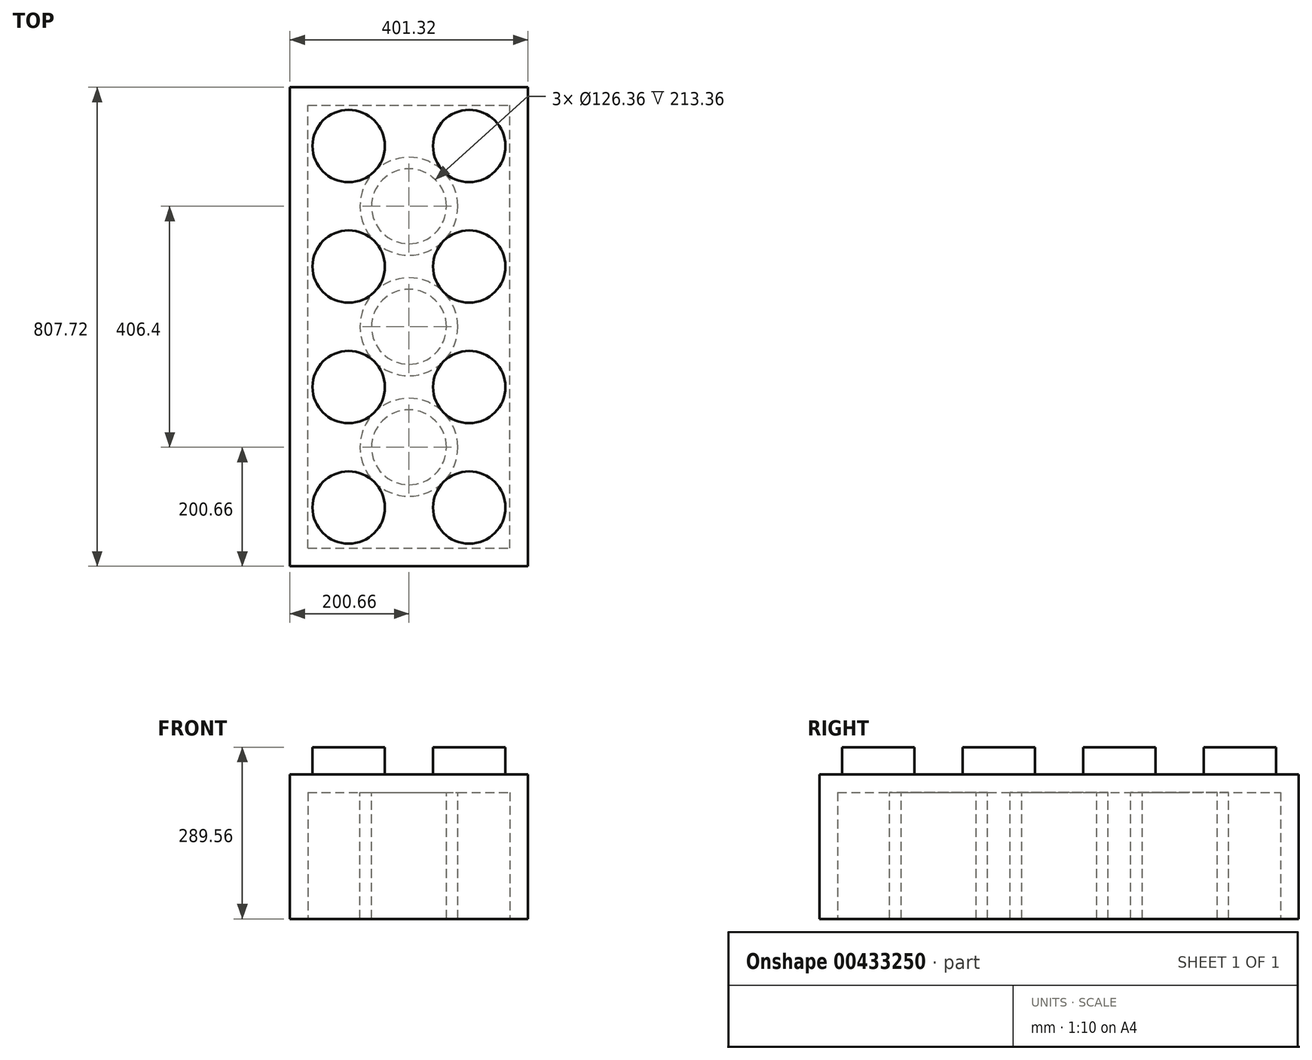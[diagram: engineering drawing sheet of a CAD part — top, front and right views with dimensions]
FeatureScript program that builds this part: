
annotation { "Feature Type Name" : "Feature", "Feature Type Description" : "" }
export const myFeature = defineFeature(function(context is Context, id is Id, definition is map)
    precondition{}
    {
        {
            var Q0;
            Q0=qCreatedBy(makeId("Top.planeOp"),FACE);
            var sketch = newSketch(context, id + "F0", { "sketchPlane" : qUnion([Q0])});
            skLineSegment(sketch, "E0.bottom", {"start": v(-200.66, -403.86) * mm, "end": v(200.66, -403.86) * mm});
            skLineSegment(sketch, "E0.top", {"start": v(-200.66, 403.86) * mm, "end": v(200.66, 403.86) * mm});
            skLineSegment(sketch, "E0.left", {"start": v(-200.66, -403.86) * mm, "end": v(-200.66, 403.86) * mm});
            skLineSegment(sketch, "E0.right", {"start": v(200.66, -403.86) * mm, "end": v(200.66, 403.86) * mm});
            skPoint(sketch, "E0.middle", {"position": v(0, 0) * mm});
            skSolve(sketch);
        }
        {
            var Q0;
            Q0 = qSketchRegion(id + "F0", true);
            extrude(context, id + "F1", {"entities" : qUnion([Q0]), "depth" : 243.84 * mm});
        }
        {
            var Q0;
            Q0=makeQuery(id+"F1.opExtrude","CAP_FACE",FACE,{"disambiguationData":[OSD([sQuery(id+"F0.wireOp",EDGE,"E0.bottom"),sQuery(id+"F0.wireOp",EDGE,"E0.top"),sQuery(id+"F0.wireOp",EDGE,"E0.left"),sQuery(id+"F0.wireOp",EDGE,"E0.right")])],"isStart":false});
            var sketch = newSketch(context, id + "F2", { "sketchPlane" : qUnion([Q0])});
            skCircle(sketch, "E1", {"center": v(101.6, 304.8) * mm, "radius": 60.96 * mm});
            skCircle(sketch, "E2.0.1.0", {"center": v(101.6, 101.6) * mm, "radius": 60.96 * mm});
            skCircle(sketch, "E2.0.2.0", {"center": v(101.6, -101.6) * mm, "radius": 60.96 * mm});
            skCircle(sketch, "E2.0.3.0", {"center": v(101.6, -304.8) * mm, "radius": 60.96 * mm});
            skCircle(sketch, "E2.1.0.0", {"center": v(-101.6, 304.8) * mm, "radius": 60.96 * mm});
            skCircle(sketch, "E2.1.1.0", {"center": v(-101.6, 101.6) * mm, "radius": 60.96 * mm});
            skCircle(sketch, "E2.1.2.0", {"center": v(-101.6, -101.6) * mm, "radius": 60.96 * mm});
            skCircle(sketch, "E2.1.3.0", {"center": v(-101.6, -304.8) * mm, "radius": 60.96 * mm});
            skLineSegment(sketch, "E2.direction1", {"start": v(101.6, 304.8) * mm, "end": v(-101.6, 304.8) * mm, "construction": true});
            skLineSegment(sketch, "E2.direction2", {"start": v(101.6, 304.8) * mm, "end": v(101.6, 101.6) * mm, "construction": true});
            skSolve(sketch);
        }
        {
            var Q0;
            Q0 = qSketchRegion(id + "F2", true);
            extrude(context, id + "F3", {"entities" : qUnion([Q0]), "operationType" : NewBodyOperationType.ADD, "depth" : 45.72 * mm});
        }
        {
            var Q0;
            Q0=makeQuery(id+"F1.opExtrude","CAP_FACE",FACE,{"disambiguationData":[OSD([sQuery(id+"F0.wireOp",EDGE,"E0.bottom"),sQuery(id+"F0.wireOp",EDGE,"E0.top"),sQuery(id+"F0.wireOp",EDGE,"E0.left"),sQuery(id+"F0.wireOp",EDGE,"E0.right")])],"isStart":true});
            var sketch = newSketch(context, id + "F4", { "sketchPlane" : qUnion([Q0])});
            skLineSegment(sketch, "E3.bottom", {"start": v(-170.18, 373.38) * mm, "end": v(170.18, 373.38) * mm});
            skLineSegment(sketch, "E3.top", {"start": v(-170.18, -373.38) * mm, "end": v(170.18, -373.38) * mm});
            skLineSegment(sketch, "E3.left", {"start": v(-170.18, 373.38) * mm, "end": v(-170.18, -373.38) * mm});
            skLineSegment(sketch, "E3.right", {"start": v(170.18, 373.38) * mm, "end": v(170.18, -373.38) * mm});
            skPoint(sketch, "E3.middle", {"position": v(0, 0) * mm});
            skSolve(sketch);
        }
        {
            var Q0;
            Q0=makeQuery(id+"F4.imprint","IMPRINT",FACE,{"disambiguationData":[TD([[makeQuery(id+"F4.imprint","IMPRINT",EDGE,{"derivedFrom":sQuery(id+"F4.wireOp",EDGE,"E3.bottom")}),-1.0]])]});
            extrude(context, id + "F5", {"entities" : qUnion([Q0]), "operationType" : NewBodyOperationType.REMOVE, "oppositeDirection" : true, "depth" : 213.36 * mm});
        }
        {
            var Q0;
            Q0=makeQuery(id+"F5.boolean.opBoolean","COPY",FACE,{"derivedFrom":makeQuery(id+"F5.opExtrude","CAP_FACE",FACE,{"disambiguationData":[OSD([sQuery(id+"F4.wireOp",EDGE,"E3.bottom"),sQuery(id+"F4.wireOp",EDGE,"E3.top"),sQuery(id+"F4.wireOp",EDGE,"E3.left"),sQuery(id+"F4.wireOp",EDGE,"E3.right")])],"isStart":false})});
            var sketch = newSketch(context, id + "F6", { "sketchPlane" : qUnion([Q0])});
            skCircle(sketch, "E4", {"center": v(0, 0) * mm, "radius": 82.55 * mm});
            skCircle(sketch, "E5", {"center": v(0, 0) * mm, "radius": 63.18 * mm});
            skCircle(sketch, "E6.0.1.0", {"center": v(0, 203.2) * mm, "radius": 82.55 * mm});
            skLineSegment(sketch, "E6.direction1", {"start": v(0, 0) * mm, "end": v(25.4, 0) * mm, "construction": true});
            skLineSegment(sketch, "E6.direction2", {"start": v(0, 0) * mm, "end": v(0, 203.2) * mm, "construction": true});
            skCircle(sketch, "E7.0.1.0", {"center": v(0, 203.2) * mm, "radius": 63.18 * mm});
            skCircle(sketch, "E8.0.1.0", {"center": v(0, -203.2) * mm, "radius": 63.18 * mm});
            skCircle(sketch, "E8.0.1.1", {"center": v(0, -203.2) * mm, "radius": 82.55 * mm});
            skLineSegment(sketch, "E8.direction1", {"start": v(0, 203.2) * mm, "end": v(25.4, 203.2) * mm, "construction": true});
            skLineSegment(sketch, "E8.direction2", {"start": v(0, 203.2) * mm, "end": v(0, -203.2) * mm, "construction": true});
            skSolve(sketch);
        }
        {
            var Q0;
            Q0 = qSketchRegion(id + "F6", true);
            var Q1;
            Q1=sQuery(id+"F6.wireOp",EDGE,"E6.0.1.0");
            var Q2;
            Q2=sQuery(id+"F6.wireOp",EDGE,"E7.0.1.0");
            var Q3;
            Q3=sQuery(id+"F6.wireOp",EDGE,"E5");
            var Q4;
            Q4=sQuery(id+"F6.wireOp",EDGE,"E4");
            var Q5;
            Q5=sQuery(id+"F6.wireOp",EDGE,"E8.0.1.0");
            var Q6;
            Q6=sQuery(id+"F6.wireOp",EDGE,"E8.0.1.1");
            extrude(context, id + "F7", {"entities" : qUnion([Q0]), "operationType" : NewBodyOperationType.ADD, "surfaceEntities" : qUnion([Q1, Q2, Q3, Q4, Q5, Q6]), "depth" : 213.36 * mm});
        }
    });
